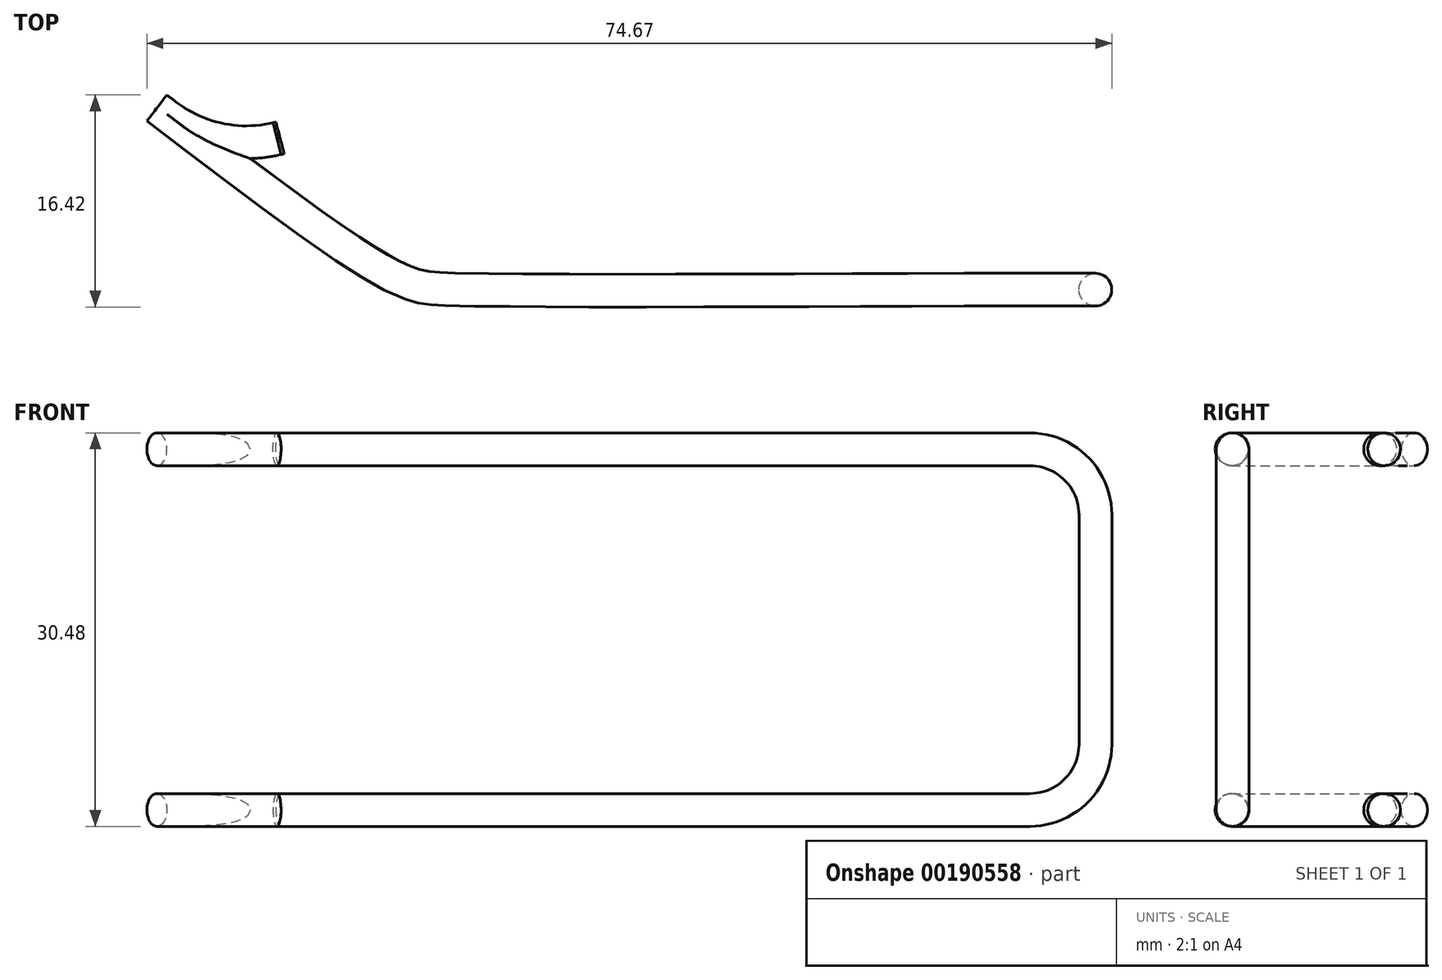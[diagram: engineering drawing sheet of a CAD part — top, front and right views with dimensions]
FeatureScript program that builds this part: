
annotation { "Feature Type Name" : "Feature", "Feature Type Description" : "" }
export const myFeature = defineFeature(function(context is Context, id is Id, definition is map)
    precondition{}
    {
        {
            var Q0;
            Q0=qCreatedBy(makeId("Top.planeOp"),FACE);
            var sketch = newSketch(context, id + "F0", { "sketchPlane" : qUnion([Q0])});
            skFitSpline(sketch, "E0", {"points": [v(0, 0) * mm, v(-39, 0) * mm, v(-43.7, 0.96) * mm, v(-61.7, 13.81) * mm], "startDerivative": vector(-103.73, -0.36) * mm, "endDerivative": vector(-60.4, 46.16) * mm});
            skFitSpline(sketch, "E1.0", {"points": [v(0, -2.54) * mm, v(-2.15, -2.55) * mm, v(-6.47, -2.56) * mm, v(-12.82, -2.58) * mm, v(-18.88, -2.6) * mm, v(-24.53, -2.6) * mm, v(-28.76, -2.6) * mm, v(-31.8, -2.6) * mm, v(-33.89, -2.6) * mm, v(-35.76, -2.58) * mm, v(-37.42, -2.56) * mm, v(-38.83, -2.54) * mm, v(-39.98, -2.52) * mm, v(-41.05, -2.47) * mm, v(-42.11, -2.33) * mm, v(-43.2, -2.04) * mm, v(-44.27, -1.61) * mm, v(-45.35, -1.06) * mm, v(-46.54, -0.36) * mm, v(-47.83, 0.46) * mm, v(-49.72, 1.72) * mm, v(-52.33, 3.57) * mm, v(-55.78, 6.13) * mm, v(-59.46, 8.9) * mm, v(-61.98, 10.83) * mm, v(-63.24, 11.8) * mm]});
            skLineSegment(sketch, "E2", {"start": v(-63.24, 11.8) * mm, "end": v(-61.7, 13.81) * mm});
            skLineSegment(sketch, "E3", {"start": v(0, 0) * mm, "end": v(0, -2.54) * mm});
            skFitSpline(sketch, "E4.0", {"points": [v(0, -1.27) * mm, v(-2.16, -1.28) * mm, v(-6.48, -1.3) * mm, v(-12.82, -1.31) * mm, v(-18.89, -1.33) * mm, v(-24.53, -1.34) * mm, v(-28.76, -1.34) * mm, v(-31.8, -1.33) * mm, v(-33.88, -1.32) * mm, v(-35.75, -1.3) * mm, v(-37.4, -1.3) * mm, v(-38.8, -1.27) * mm, v(-39.95, -1.25) * mm, v(-40.77, -1.2) * mm, v(-41.4, -1.14) * mm, v(-42.03, -1.04) * mm, v(-42.65, -0.87) * mm, v(-43.26, -0.65) * mm, v(-43.9, -0.37) * mm, v(-44.73, 0.05) * mm, v(-45.87, 0.72) * mm, v(-47.14, 1.52) * mm, v(-49, 2.76) * mm, v(-51.58, 4.6) * mm, v(-55.02, 7.14) * mm, v(-58.69, 9.92) * mm, v(-61.2, 11.84) * mm, v(-62.47, 12.8) * mm]});
            skLineSegment(sketch, "E5", {"start": v(-62.47, 12.8) * mm, "end": v(-66.56, 15.93) * mm});
            skLineSegment(sketch, "E6", {"start": v(0, -1.27) * mm, "end": v(2.3, -1.27) * mm});
            skSolve(sketch);
        }
        {
            var Q0;
            Q0=qCreatedBy(makeId("Right.planeOp"),FACE);
            var sketch = newSketch(context, id + "F1", { "sketchPlane" : qUnion([Q0])});
            skCircle(sketch, "E7", {"center": v(-1.27, 0) * mm, "radius": 1.27 * mm});
            skSolve(sketch);
        }
        {
            var Q0;
            Q0=makeQuery(id+"F1.imprint","IMPRINT",FACE,{"disambiguationData":[TD([[makeQuery(id+"F1.imprint","IMPRINT",EDGE,{"derivedFrom":sQuery(id+"F1.wireOp",EDGE,"E7")}),1.0]])]});
            var Q1;
            Q1=sQuery(id+"F0.wireOp",EDGE,"E4.0");
            sweep(context, id + "F2", {"profiles" : qUnion([Q0]), "path" : qUnion([Q1])});
        }
        {
            var Q0;
            Q0=qCreatedBy(makeId("Front.planeOp"),FACE);
            var sketch = newSketch(context, id + "F3", { "sketchPlane" : qUnion([Q0])});
            skLineSegment(sketch, "E8", {"start": v(0, 0) * mm, "end": v(5.08, 0) * mm});
            skLineSegment(sketch, "E9", {"start": v(10.16, -5.08) * mm, "end": v(10.16, -13.97) * mm});
            skPoint(sketch, "E10.visualSharp", {"position": v(10.16, 0) * mm});
            skArc(sketch, "E10.filletArc", {"start": v(10.16, -5.08) * mm, "mid": v(8.67, -1.49) * mm, "end": v(5.08, 0) * mm});
            skSolve(sketch);
        }
        {
            var Q0;
            Q0=makeQuery(id+"F2.opSweep","CAP_FACE",FACE,{"disambiguationData":[OSD([sQuery(id+"F0.wireOp",VERTEX,"E4.0.start"),sQuery(id+"F1.wireOp",EDGE,"E7")])],"isStart":true});
            var Q1;
            Q1=sQuery(id+"F3.wireOp",EDGE,"E8");
            var Q2;
            Q2=sQuery(id+"F3.wireOp",EDGE,"E10.filletArc");
            var Q3;
            Q3=sQuery(id+"F3.wireOp",EDGE,"E9");
            sweep(context, id + "F4", {"operationType" : NewBodyOperationType.ADD, "profiles" : qUnion([Q0]), "path" : qUnion([Q1, Q2, Q3])});
        }
        {
            var Q0;
            Q0=makeQuery(id+"F2.opSweep","CAP_FACE",FACE,{"disambiguationData":[OSD([sQuery(id+"F0.wireOp",VERTEX,"E4.0.end"),sQuery(id+"F1.wireOp",EDGE,"E7")])],"isStart":false});
            var sketch = newSketch(context, id + "F5", { "sketchPlane" : qUnion([Q0])});
            skSolve(sketch);
        }
        {
            var Q0;
            {var subQ0=sQuery(id+"F0.wireOp",EDGE,"E1.0");Q0=makeQuery(id+"F0.imprint","IMPRINT",FACE,{"disambiguationData":[TD([[makeQuery(id+"F0.imprint","IMPRINT",EDGE,{"derivedFrom":subQ0}),-1.0]])]});}
            var sketch = newSketch(context, id + "F6", { "sketchPlane" : qUnion([Q0])});
            skLineSegment(sketch, "E11", {"start": v(-62.47, 12.8) * mm, "end": v(-61.7, 13.81) * mm});
            skLineSegment(sketch, "E12", {"start": v(-62.47, 12.8) * mm, "end": v(-61.73, 12.24) * mm});
            skLineSegment(sketch, "E13", {"start": v(-53.17, 10.43) * mm, "end": v(-52.94, 10.49) * mm});
            skPoint(sketch, "E13.endSnap0", {"position": v(-59.44, 10.49) * mm});
            skPoint(sketch, "E14.newPointA", {"position": v(-56.41, 8.17) * mm});
            skPoint(sketch, "E14.newPointB", {"position": v(-57.88, 9.3) * mm});
            skArc(sketch, "E14.filletArc", {"start": v(-61.73, 12.24) * mm, "mid": v(-57.66, 10.37) * mm, "end": v(-53.17, 10.43) * mm});
            skSolve(sketch);
        }
        {
            var Q0;
            Q0=makeQuery(id+"F5.imprint","IMPRINT",FACE,{"disambiguationData":[TD([[makeQuery(id+"F5.imprint","IMPRINT",EDGE,{"derivedFrom":makeQuery(id+"F2.opSweep","CAP_EDGE",EDGE,{"disambiguationData":[OSD([sQuery(id+"F0.wireOp",VERTEX,"E4.0.end"),sQuery(id+"F1.wireOp",EDGE,"E7")])],"isStart":false})}),1.0]])]});
            var Q1;
            Q1=sQuery(id+"F6.wireOp",EDGE,"E14.filletArc");
            var Q2;
            Q2=sQuery(id+"F6.wireOp",EDGE,"E12");
            var Q3;
            Q3=sQuery(id+"F6.wireOp",EDGE,"E13");
            sweep(context, id + "F7", {"operationType" : NewBodyOperationType.ADD, "profiles" : qUnion([Q0]), "path" : qUnion([Q1, Q2, Q3])});
        }
        {
            var Q0;
            Q0=makeQuery(id+"F2.opSweep","SWEPT_BODY",BODY,{"disambiguationData":[OSD([sQuery(id+"F0.wireOp",EDGE,"E4.0"),sQuery(id+"F1.wireOp",EDGE,"E7")])]});
            var Q1;
            Q1=makeQuery(id+"F4.opSweep","CAP_FACE",FACE,{"disambiguationData":[OSD([sQuery(id+"F0.wireOp",VERTEX,"E4.0.start"),sQuery(id+"F1.wireOp",EDGE,"E7"),sQuery(id+"F3.wireOp",VERTEX,"E9.end")])],"isStart":false});
            mirror(context, id + "F8", {"operationType" : NewBodyOperationType.ADD, "entities" : qUnion([Q0]), "mirrorPlane" : qUnion([Q1])});
        }
    });
